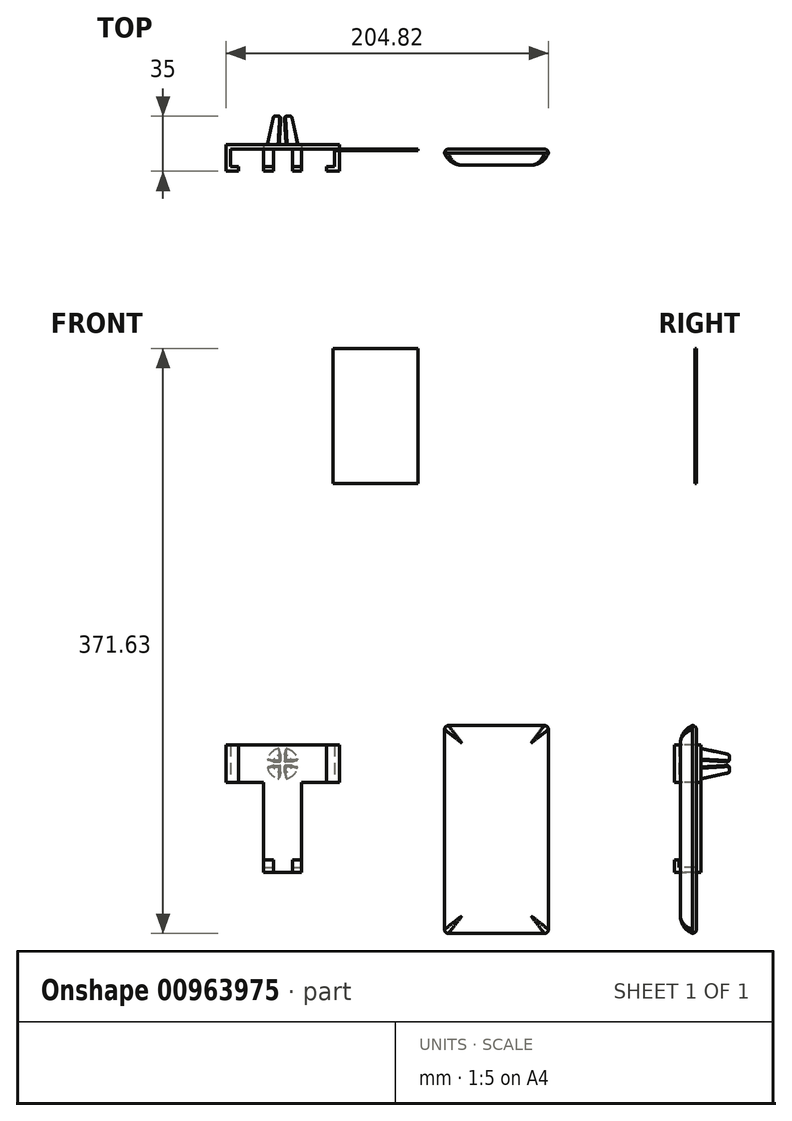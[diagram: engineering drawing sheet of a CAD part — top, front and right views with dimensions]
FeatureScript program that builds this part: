
annotation { "Feature Type Name" : "Feature", "Feature Type Description" : "" }
export const myFeature = defineFeature(function(context is Context, id is Id, definition is map)
    precondition{}
    {
        {
            var Q0;
            Q0=qCreatedBy(makeId("Front.planeOp"),FACE);
            var sketch = newSketch(context, id + "F0", { "sketchPlane" : qUnion([Q0])});
            skCircle(sketch, "E0", {"center": v(0, 0) * mm, "radius": 10 * mm});
            skSolve(sketch);
        }
        {
            var Q0;
            Q0=qSketchRegion(id+"F0",true);
            extrude(context, id + "F1", {"entities" : qUnion([Q0]), "oppositeDirection" : true, "depth" : 3 * mm});
        }
        {
            var Q0;
            Q0=makeQuery(id+"F1.opExtrude","CAP_FACE",FACE,{"disambiguationData":[OSD([sQuery(id+"F0.wireOp",EDGE,"E0")])],"isStart":false});
            var sketch = newSketch(context, id + "F2", { "sketchPlane" : qUnion([Q0])});
            skLineSegment(sketch, "E1.top", {"start": v(-9.75, 2.2) * mm, "end": v(-2.2, 2.2) * mm});
            skLineSegment(sketch, "E1.right", {"start": v(-2.2, 9.75) * mm, "end": v(-2.2, 2.2) * mm});
            skArc(sketch, "E2", {"start": v(-2.2, 9.75) * mm, "mid": v(-7.07, 7.07) * mm, "end": v(-9.75, 2.2) * mm});
            skLineSegment(sketch, "E3.1.0", {"start": v(-9.75, -2.2) * mm, "end": v(-2.2, -2.2) * mm});
            skLineSegment(sketch, "E3.1.1", {"start": v(-2.2, -9.75) * mm, "end": v(-2.2, -2.2) * mm});
            skArc(sketch, "E3.1.2", {"start": v(-9.75, -2.2) * mm, "mid": v(-7.07, -7.07) * mm, "end": v(-2.2, -9.75) * mm});
            skLineSegment(sketch, "E3.2.0", {"start": v(2.2, -9.75) * mm, "end": v(2.2, -2.2) * mm});
            skLineSegment(sketch, "E3.2.1", {"start": v(9.75, -2.2) * mm, "end": v(2.2, -2.2) * mm});
            skArc(sketch, "E3.2.2", {"start": v(2.2, -9.75) * mm, "mid": v(7.07, -7.07) * mm, "end": v(9.75, -2.2) * mm});
            skLineSegment(sketch, "E4.2.3.0", {"start": v(9.75, 2.2) * mm, "end": v(2.2, 2.2) * mm});
            skLineSegment(sketch, "E4.3.3.0", {"start": v(2.2, 9.75) * mm, "end": v(2.2, 2.2) * mm});
            skArc(sketch, "E4.6.3.0", {"start": v(9.75, 2.2) * mm, "mid": v(7.07, 7.07) * mm, "end": v(2.2, 9.75) * mm});
            skSolve(sketch);
        }
        {
            var Q0;
            Q0=makeQuery(id+"F2.imprint","IMPRINT",FACE,{"disambiguationData":[TD([[makeQuery(id+"F2.imprint","IMPRINT",EDGE,{"derivedFrom":sQuery(id+"F2.wireOp",EDGE,"E1.top")}),-1.0]])]});
            cPlane(context, id + "F3", {"entities" : qUnion([Q0]), "cplaneType" : CPlaneType.OFFSET, "offset" : 18 * mm, "width" : 150 * mm, "height" : 150 * mm});
        }
        {
            var Q0;
            Q0=qCreatedBy(id+"F3.planeOp",FACE);
            var sketch = newSketch(context, id + "F4", { "sketchPlane" : qUnion([Q0])});
            skLineSegment(sketch, "E5.top", {"start": v(-5.9, 1.1) * mm, "end": v(-1.1, 1.1) * mm});
            skLineSegment(sketch, "E5.right", {"start": v(-1.1, 5.9) * mm, "end": v(-1.1, 1.1) * mm});
            skArc(sketch, "E6", {"start": v(-1.1, 5.9) * mm, "mid": v(-4.24, 4.24) * mm, "end": v(-5.9, 1.1) * mm});
            skLineSegment(sketch, "E7.1.0", {"start": v(-5.9, -1.1) * mm, "end": v(-1.1, -1.1) * mm});
            skLineSegment(sketch, "E7.1.1", {"start": v(-1.1, -5.9) * mm, "end": v(-1.1, -1.1) * mm});
            skArc(sketch, "E7.1.2", {"start": v(-5.9, -1.1) * mm, "mid": v(-4.24, -4.24) * mm, "end": v(-1.1, -5.9) * mm});
            skLineSegment(sketch, "E7.2.0", {"start": v(1.1, -5.9) * mm, "end": v(1.1, -1.1) * mm});
            skLineSegment(sketch, "E7.2.1", {"start": v(5.9, -1.1) * mm, "end": v(1.1, -1.1) * mm});
            skArc(sketch, "E7.2.2", {"start": v(1.1, -5.9) * mm, "mid": v(4.24, -4.24) * mm, "end": v(5.9, -1.1) * mm});
            skLineSegment(sketch, "E7.3.0", {"start": v(5.9, 1.1) * mm, "end": v(1.1, 1.1) * mm});
            skLineSegment(sketch, "E7.3.1", {"start": v(1.1, 5.9) * mm, "end": v(1.1, 1.1) * mm});
            skArc(sketch, "E7.3.2", {"start": v(5.9, 1.1) * mm, "mid": v(4.24, 4.24) * mm, "end": v(1.1, 5.9) * mm});
            skSolve(sketch);
        }
        {
            var Q1;
            Q1=makeQuery(id+"F4.imprint","IMPRINT",FACE,{"disambiguationData":[TD([[makeQuery(id+"F4.imprint","IMPRINT",EDGE,{"derivedFrom":sQuery(id+"F4.wireOp",EDGE,"E5.top")}),1.0]])]});
            var Q2;
            Q2=makeQuery(id+"F2.imprint","IMPRINT",FACE,{"disambiguationData":[TD([[makeQuery(id+"F2.imprint","IMPRINT",EDGE,{"derivedFrom":sQuery(id+"F2.wireOp",EDGE,"E1.top")}),1.0]])]});
            loft(context, id + "F5", {"operationType" : NewBodyOperationType.ADD, "sheetProfilesArray" : [{ "sheetProfileEntities" : qUnion([Q1]) }, { "sheetProfileEntities" : qUnion([Q2]) }]});
        }
        {
            var Q1;
            Q1=makeQuery(id+"F2.imprint","IMPRINT",FACE,{"disambiguationData":[TD([[makeQuery(id+"F2.imprint","IMPRINT",EDGE,{"derivedFrom":sQuery(id+"F2.wireOp",EDGE,"E4.2.3.0")}),-1.0]])]});
            var Q2;
            Q2=makeQuery(id+"F4.imprint","IMPRINT",FACE,{"disambiguationData":[TD([[makeQuery(id+"F4.imprint","IMPRINT",EDGE,{"derivedFrom":sQuery(id+"F4.wireOp",EDGE,"E7.3.0")}),-1.0]])]});
            loft(context, id + "F6", {"operationType" : NewBodyOperationType.ADD, "sheetProfilesArray" : [{ "sheetProfileEntities" : qUnion([Q1]) }, { "sheetProfileEntities" : qUnion([Q2]) }]});
        }
        {
            var Q1;
            Q1=makeQuery(id+"F2.imprint","IMPRINT",FACE,{"disambiguationData":[TD([[makeQuery(id+"F2.imprint","IMPRINT",EDGE,{"derivedFrom":sQuery(id+"F2.wireOp",EDGE,"E3.1.0")}),-1.0]])]});
            var Q2;
            Q2=makeQuery(id+"F4.imprint","IMPRINT",FACE,{"disambiguationData":[TD([[makeQuery(id+"F4.imprint","IMPRINT",EDGE,{"derivedFrom":sQuery(id+"F4.wireOp",EDGE,"E7.1.0")}),-1.0]])]});
            loft(context, id + "F7", {"operationType" : NewBodyOperationType.ADD, "sheetProfilesArray" : [{ "sheetProfileEntities" : qUnion([Q1]) }, { "sheetProfileEntities" : qUnion([Q2]) }]});
        }
        {
            var Q1;
            Q1=makeQuery(id+"F2.imprint","IMPRINT",FACE,{"disambiguationData":[TD([[makeQuery(id+"F2.imprint","IMPRINT",EDGE,{"derivedFrom":sQuery(id+"F2.wireOp",EDGE,"E3.2.0")}),-1.0]])]});
            var Q2;
            Q2=makeQuery(id+"F4.imprint","IMPRINT",FACE,{"disambiguationData":[TD([[makeQuery(id+"F4.imprint","IMPRINT",EDGE,{"derivedFrom":sQuery(id+"F4.wireOp",EDGE,"E7.2.0")}),-1.0]])]});
            loft(context, id + "F8", {"operationType" : NewBodyOperationType.ADD, "sheetProfilesArray" : [{ "sheetProfileEntities" : qUnion([Q1]) }, { "sheetProfileEntities" : qUnion([Q2]) }]});
        }
        {
            var Q0;
            {var subQ0=sQuery(id+"F4.wireOp",EDGE,"E6");var subQ1=sQuery(id+"F4.wireOp",EDGE,"E5.right");var subQ2=sQuery(id+"F4.wireOp",EDGE,"E5.top");Q0=makeQuery(id+"F5.opLoft","MID_CAP_EDGE",EDGE,{"disambiguationData":[OSD([subQ2,subQ1,subQ0]),TDD([makeQuery(id+"F4.imprint","INTERSECT",VERTEX,{"derivedFrom":[subQ2,subQ0]}),makeQuery(id+"F4.imprint","INTERSECT",VERTEX,{"derivedFrom":[subQ1,subQ0]}),makeQuery(id+"F4.imprint","IMPRINT",EDGE,{"derivedFrom":subQ0})])],"capPos":0.0});}
            var Q1;
            Q1=makeQuery(id+"F5.opLoft","SWEPT_EDGE",EDGE,{"disambiguationData":[OSD([sQuery(id+"F2.wireOp",EDGE,"E1.right"),sQuery(id+"F2.wireOp",EDGE,"E2"),sQuery(id+"F4.wireOp",EDGE,"E5.right"),sQuery(id+"F4.wireOp",EDGE,"E6")])]});
            var Q2;
            Q2=makeQuery(id+"F5.opLoft","SWEPT_EDGE",EDGE,{"disambiguationData":[OSD([sQuery(id+"F2.wireOp",EDGE,"E1.top"),sQuery(id+"F2.wireOp",EDGE,"E1.right"),sQuery(id+"F4.wireOp",EDGE,"E5.top"),sQuery(id+"F4.wireOp",EDGE,"E5.right")])]});
            var Q3;
            Q3=makeQuery(id+"F5.opLoft","SWEPT_EDGE",EDGE,{"disambiguationData":[OSD([sQuery(id+"F2.wireOp",EDGE,"E1.top"),sQuery(id+"F2.wireOp",EDGE,"E2"),sQuery(id+"F4.wireOp",EDGE,"E5.top"),sQuery(id+"F4.wireOp",EDGE,"E6")])]});
            var Q4;
            {var subQ0=sQuery(id+"F4.wireOp",EDGE,"E7.1.2");var subQ1=sQuery(id+"F4.wireOp",EDGE,"E7.1.1");var subQ2=sQuery(id+"F4.wireOp",EDGE,"E7.1.0");Q4=makeQuery(id+"F7.opLoft","MID_CAP_EDGE",EDGE,{"disambiguationData":[OSD([subQ2,subQ1,subQ0]),TDD([makeQuery(id+"F4.imprint","INTERSECT",VERTEX,{"derivedFrom":[subQ2,subQ0]}),makeQuery(id+"F4.imprint","INTERSECT",VERTEX,{"derivedFrom":[subQ1,subQ0]}),makeQuery(id+"F4.imprint","IMPRINT",EDGE,{"derivedFrom":subQ0})])],"capPos":1.0});}
            var Q5;
            Q5=makeQuery(id+"F7.opLoft","SWEPT_EDGE",EDGE,{"disambiguationData":[OSD([sQuery(id+"F2.wireOp",EDGE,"E3.1.0"),sQuery(id+"F2.wireOp",EDGE,"E3.1.2"),sQuery(id+"F4.wireOp",EDGE,"E7.1.0"),sQuery(id+"F4.wireOp",EDGE,"E7.1.2")])]});
            var Q6;
            Q6=makeQuery(id+"F7.opLoft","SWEPT_EDGE",EDGE,{"disambiguationData":[OSD([sQuery(id+"F2.wireOp",EDGE,"E3.1.0"),sQuery(id+"F2.wireOp",EDGE,"E3.1.1"),sQuery(id+"F4.wireOp",EDGE,"E7.1.0"),sQuery(id+"F4.wireOp",EDGE,"E7.1.1")])]});
            var Q7;
            Q7=makeQuery(id+"F7.opLoft","SWEPT_EDGE",EDGE,{"disambiguationData":[OSD([sQuery(id+"F2.wireOp",EDGE,"E3.1.1"),sQuery(id+"F2.wireOp",EDGE,"E3.1.2"),sQuery(id+"F4.wireOp",EDGE,"E7.1.1"),sQuery(id+"F4.wireOp",EDGE,"E7.1.2")])]});
            var Q8;
            {var subQ0=sQuery(id+"F4.wireOp",EDGE,"E7.2.2");var subQ1=sQuery(id+"F4.wireOp",EDGE,"E7.2.1");var subQ2=sQuery(id+"F4.wireOp",EDGE,"E7.2.0");Q8=makeQuery(id+"F8.opLoft","MID_CAP_EDGE",EDGE,{"disambiguationData":[OSD([subQ2,subQ1,subQ0]),TDD([makeQuery(id+"F4.imprint","INTERSECT",VERTEX,{"derivedFrom":[subQ2,subQ0]}),makeQuery(id+"F4.imprint","INTERSECT",VERTEX,{"derivedFrom":[subQ1,subQ0]}),makeQuery(id+"F4.imprint","IMPRINT",EDGE,{"derivedFrom":subQ0})])],"capPos":1.0});}
            var Q9;
            Q9=makeQuery(id+"F8.opLoft","SWEPT_EDGE",EDGE,{"disambiguationData":[OSD([sQuery(id+"F2.wireOp",EDGE,"E3.2.0"),sQuery(id+"F2.wireOp",EDGE,"E3.2.2"),sQuery(id+"F4.wireOp",EDGE,"E7.2.0"),sQuery(id+"F4.wireOp",EDGE,"E7.2.2")])]});
            var Q10;
            Q10=makeQuery(id+"F8.opLoft","SWEPT_EDGE",EDGE,{"disambiguationData":[OSD([sQuery(id+"F2.wireOp",EDGE,"E3.2.1"),sQuery(id+"F2.wireOp",EDGE,"E3.2.2"),sQuery(id+"F4.wireOp",EDGE,"E7.2.1"),sQuery(id+"F4.wireOp",EDGE,"E7.2.2")])]});
            var Q11;
            Q11=makeQuery(id+"F8.opLoft","SWEPT_EDGE",EDGE,{"disambiguationData":[OSD([sQuery(id+"F2.wireOp",EDGE,"E3.2.0"),sQuery(id+"F2.wireOp",EDGE,"E3.2.1"),sQuery(id+"F4.wireOp",EDGE,"E7.2.0"),sQuery(id+"F4.wireOp",EDGE,"E7.2.1")])]});
            var Q12;
            {var subQ0=sQuery(id+"F4.wireOp",EDGE,"E7.3.2");var subQ1=sQuery(id+"F4.wireOp",EDGE,"E7.3.1");var subQ2=sQuery(id+"F4.wireOp",EDGE,"E7.3.0");Q12=makeQuery(id+"F6.opLoft","MID_CAP_EDGE",EDGE,{"disambiguationData":[OSD([subQ2,subQ1,subQ0]),TDD([makeQuery(id+"F4.imprint","INTERSECT",VERTEX,{"derivedFrom":[subQ2,subQ0]}),makeQuery(id+"F4.imprint","INTERSECT",VERTEX,{"derivedFrom":[subQ1,subQ0]}),makeQuery(id+"F4.imprint","IMPRINT",EDGE,{"derivedFrom":subQ0})])],"capPos":1.0});}
            var Q13;
            Q13=makeQuery(id+"F6.opLoft","SWEPT_EDGE",EDGE,{"disambiguationData":[OSD([sQuery(id+"F2.wireOp",EDGE,"E4.2.3.0"),sQuery(id+"F2.wireOp",EDGE,"E4.3.3.0"),sQuery(id+"F4.wireOp",EDGE,"E7.3.0"),sQuery(id+"F4.wireOp",EDGE,"E7.3.1")])]});
            var Q14;
            Q14=makeQuery(id+"F6.opLoft","SWEPT_EDGE",EDGE,{"disambiguationData":[OSD([sQuery(id+"F2.wireOp",EDGE,"E4.2.3.0"),sQuery(id+"F2.wireOp",EDGE,"E4.6.3.0"),sQuery(id+"F4.wireOp",EDGE,"E7.3.0"),sQuery(id+"F4.wireOp",EDGE,"E7.3.2")])]});
            var Q15;
            Q15=makeQuery(id+"F6.opLoft","SWEPT_EDGE",EDGE,{"disambiguationData":[OSD([sQuery(id+"F2.wireOp",EDGE,"E4.3.3.0"),sQuery(id+"F2.wireOp",EDGE,"E4.6.3.0"),sQuery(id+"F4.wireOp",EDGE,"E7.3.1"),sQuery(id+"F4.wireOp",EDGE,"E7.3.2")])]});
            fillet(context, id + "F9", {"entities" : qUnion([Q0, Q1, Q2, Q3, Q4, Q5, Q6, Q7, Q8, Q9, Q10, Q11, Q12, Q13, Q14, Q15]), "radius" : .5 * mm, "tangentPropagation" : true, "allowEdgeOverflow" : false});
        }
        {
            var Q0;
            Q0=qCreatedBy(makeId("Front.planeOp"),FACE);
            var sketch = newSketch(context, id + "F10", { "sketchPlane" : qUnion([Q0])});
            skLineSegment(sketch, "E8.bottom", {"start": v(86.03, 177.78) * mm, "end": v(32.03, 177.78) * mm});
            skLineSegment(sketch, "E8.top", {"start": v(86.03, 263.78) * mm, "end": v(32.03, 263.78) * mm});
            skLineSegment(sketch, "E8.left", {"start": v(86.03, 177.78) * mm, "end": v(86.03, 263.78) * mm});
            skLineSegment(sketch, "E8.right", {"start": v(32.03, 177.78) * mm, "end": v(32.03, 263.78) * mm});
            skSolve(sketch);
        }
        {
            var Q0;
            Q0=makeQuery(id+"F10.imprint","IMPRINT",FACE,{"disambiguationData":[TD([[makeQuery(id+"F10.imprint","IMPRINT",EDGE,{"derivedFrom":sQuery(id+"F10.wireOp",EDGE,"E8.bottom")}),-1.0]])]});
            extrude(context, id + "F11", {"entities" : qUnion([Q0]), "depth" : 1 * mm});
        }
        {
            var Q0;
            {var subQ0=sQuery(id+"F4.wireOp",EDGE,"E5.right");var subQ1=sQuery(id+"F4.wireOp",EDGE,"E6");var subQ2=sQuery(id+"F4.wireOp",EDGE,"E5.top");Q0=makeQuery(id+"F5.opLoft","MID_CAP_EDGE",EDGE,{"disambiguationData":[OSD([subQ2,subQ0,subQ1]),TDD([makeQuery(id+"F4.imprint","INTERSECT",VERTEX,{"derivedFrom":[subQ2,subQ0]}),makeQuery(id+"F4.imprint","INTERSECT",VERTEX,{"derivedFrom":[subQ0,subQ1]}),makeQuery(id+"F4.imprint","IMPRINT",EDGE,{"derivedFrom":subQ0})])],"capPos":0.0});}
            var Q1;
            {var subQ0=sQuery(id+"F4.wireOp",EDGE,"E5.top");var subQ1=sQuery(id+"F4.wireOp",EDGE,"E5.right");var subQ2=sQuery(id+"F4.wireOp",EDGE,"E6");Q1=makeQuery(id+"F5.opLoft","MID_CAP_EDGE",EDGE,{"disambiguationData":[OSD([subQ0,subQ1,subQ2]),TDD([makeQuery(id+"F4.imprint","INTERSECT",VERTEX,{"derivedFrom":[subQ0,subQ2]}),makeQuery(id+"F4.imprint","INTERSECT",VERTEX,{"derivedFrom":[subQ0,subQ1]}),makeQuery(id+"F4.imprint","IMPRINT",EDGE,{"derivedFrom":subQ0})])],"capPos":0.0});}
            var Q2;
            {var subQ0=sQuery(id+"F4.wireOp",EDGE,"E7.1.0");var subQ1=sQuery(id+"F4.wireOp",EDGE,"E7.1.1");var subQ2=sQuery(id+"F4.wireOp",EDGE,"E7.1.2");Q2=makeQuery(id+"F7.opLoft","MID_CAP_EDGE",EDGE,{"disambiguationData":[OSD([subQ0,subQ1,subQ2]),TDD([makeQuery(id+"F4.imprint","INTERSECT",VERTEX,{"derivedFrom":[subQ0,subQ2]}),makeQuery(id+"F4.imprint","INTERSECT",VERTEX,{"derivedFrom":[subQ0,subQ1]}),makeQuery(id+"F4.imprint","IMPRINT",EDGE,{"derivedFrom":subQ0})])],"capPos":1.0});}
            var Q3;
            {var subQ0=sQuery(id+"F4.wireOp",EDGE,"E7.1.1");var subQ1=sQuery(id+"F4.wireOp",EDGE,"E7.1.2");var subQ2=sQuery(id+"F4.wireOp",EDGE,"E7.1.0");Q3=makeQuery(id+"F7.opLoft","MID_CAP_EDGE",EDGE,{"disambiguationData":[OSD([subQ2,subQ0,subQ1]),TDD([makeQuery(id+"F4.imprint","INTERSECT",VERTEX,{"derivedFrom":[subQ2,subQ0]}),makeQuery(id+"F4.imprint","INTERSECT",VERTEX,{"derivedFrom":[subQ0,subQ1]}),makeQuery(id+"F4.imprint","IMPRINT",EDGE,{"derivedFrom":subQ0})])],"capPos":1.0});}
            var Q4;
            {var subQ0=sQuery(id+"F4.wireOp",EDGE,"E7.2.0");var subQ1=sQuery(id+"F4.wireOp",EDGE,"E7.2.1");var subQ2=sQuery(id+"F4.wireOp",EDGE,"E7.2.2");Q4=makeQuery(id+"F8.opLoft","MID_CAP_EDGE",EDGE,{"disambiguationData":[OSD([subQ0,subQ1,subQ2]),TDD([makeQuery(id+"F4.imprint","INTERSECT",VERTEX,{"derivedFrom":[subQ0,subQ2]}),makeQuery(id+"F4.imprint","INTERSECT",VERTEX,{"derivedFrom":[subQ0,subQ1]}),makeQuery(id+"F4.imprint","IMPRINT",EDGE,{"derivedFrom":subQ0})])],"capPos":1.0});}
            var Q5;
            {var subQ0=sQuery(id+"F4.wireOp",EDGE,"E7.2.1");var subQ1=sQuery(id+"F4.wireOp",EDGE,"E7.2.2");var subQ2=sQuery(id+"F4.wireOp",EDGE,"E7.2.0");Q5=makeQuery(id+"F8.opLoft","MID_CAP_EDGE",EDGE,{"disambiguationData":[OSD([subQ2,subQ0,subQ1]),TDD([makeQuery(id+"F4.imprint","INTERSECT",VERTEX,{"derivedFrom":[subQ2,subQ0]}),makeQuery(id+"F4.imprint","INTERSECT",VERTEX,{"derivedFrom":[subQ0,subQ1]}),makeQuery(id+"F4.imprint","IMPRINT",EDGE,{"derivedFrom":subQ0})])],"capPos":1.0});}
            var Q6;
            {var subQ0=sQuery(id+"F4.wireOp",EDGE,"E7.3.0");var subQ1=sQuery(id+"F4.wireOp",EDGE,"E7.3.1");var subQ2=sQuery(id+"F4.wireOp",EDGE,"E7.3.2");Q6=makeQuery(id+"F6.opLoft","MID_CAP_EDGE",EDGE,{"disambiguationData":[OSD([subQ0,subQ1,subQ2]),TDD([makeQuery(id+"F4.imprint","INTERSECT",VERTEX,{"derivedFrom":[subQ0,subQ2]}),makeQuery(id+"F4.imprint","INTERSECT",VERTEX,{"derivedFrom":[subQ0,subQ1]}),makeQuery(id+"F4.imprint","IMPRINT",EDGE,{"derivedFrom":subQ0})])],"capPos":1.0});}
            var Q7;
            {var subQ0=sQuery(id+"F4.wireOp",EDGE,"E7.3.1");var subQ1=sQuery(id+"F4.wireOp",EDGE,"E7.3.2");var subQ2=sQuery(id+"F4.wireOp",EDGE,"E7.3.0");Q7=makeQuery(id+"F6.opLoft","MID_CAP_EDGE",EDGE,{"disambiguationData":[OSD([subQ2,subQ0,subQ1]),TDD([makeQuery(id+"F4.imprint","INTERSECT",VERTEX,{"derivedFrom":[subQ2,subQ0]}),makeQuery(id+"F4.imprint","INTERSECT",VERTEX,{"derivedFrom":[subQ0,subQ1]}),makeQuery(id+"F4.imprint","IMPRINT",EDGE,{"derivedFrom":subQ0})])],"capPos":1.0});}
            fillet(context, id + "F12", {"entities" : qUnion([Q0, Q1, Q2, Q3, Q4, Q5, Q6, Q7]), "radius" : 1.5 * mm, "tangentPropagation" : true, "allowEdgeOverflow" : false});
        }
        {
            var Q0;
            Q0=qCreatedBy(makeId("Front.planeOp"),FACE);
            var sketch = newSketch(context, id + "F13", { "sketchPlane" : qUnion([Q0])});
            skLineSegment(sketch, "E9.bottom", {"start": v(102.82, 24.15) * mm, "end": v(168.82, 24.15) * mm});
            skLineSegment(sketch, "E9.top", {"start": v(102.82, -107.85) * mm, "end": v(168.82, -107.85) * mm});
            skLineSegment(sketch, "E9.left", {"start": v(102.82, 24.15) * mm, "end": v(102.82, -107.85) * mm});
            skLineSegment(sketch, "E9.right", {"start": v(168.82, 24.15) * mm, "end": v(168.82, -107.85) * mm});
            skSolve(sketch);
        }
        {
            var Q0;
            Q0=qSketchRegion(id+"F13",true);
            extrude(context, id + "F14", {"entities" : qUnion([Q0]), "depth" : 10.16 * mm});
        }
        {
            var Q0;
            Q0=makeQuery(id+"F14.opExtrude","SWEPT_EDGE",EDGE,{"disambiguationData":[OSD([sQuery(id+"F13.wireOp",EDGE,"E9.bottom"),sQuery(id+"F13.wireOp",EDGE,"E9.left")])]});
            var Q1;
            Q1=makeQuery(id+"F14.opExtrude","SWEPT_EDGE",EDGE,{"disambiguationData":[OSD([sQuery(id+"F13.wireOp",EDGE,"E9.bottom"),sQuery(id+"F13.wireOp",EDGE,"E9.right")])]});
            var Q2;
            Q2=makeQuery(id+"F14.opExtrude","SWEPT_EDGE",EDGE,{"disambiguationData":[OSD([sQuery(id+"F13.wireOp",EDGE,"E9.top"),sQuery(id+"F13.wireOp",EDGE,"E9.right")])]});
            var Q3;
            Q3=makeQuery(id+"F14.opExtrude","SWEPT_EDGE",EDGE,{"disambiguationData":[OSD([sQuery(id+"F13.wireOp",EDGE,"E9.top"),sQuery(id+"F13.wireOp",EDGE,"E9.left")])]});
            fillet(context, id + "F15", {"entities" : qUnion([Q0, Q1, Q2, Q3]), "radius" : 2.5 * mm, "tangentPropagation" : true, "allowEdgeOverflow" : false});
        }
        {
            var Q0;
            Q0=makeQuery(id+"F14.opExtrude","CAP_EDGE",EDGE,{"disambiguationData":[OSD([sQuery(id+"F13.wireOp",EDGE,"E9.right")])],"isStart":true});
            var Q1;
            Q1=makeQuery(id+"F14.opExtrude","CAP_EDGE",EDGE,{"disambiguationData":[OSD([sQuery(id+"F13.wireOp",EDGE,"E9.bottom")])],"isStart":true});
            var Q2;
            Q2=makeQuery(id+"F14.opExtrude","CAP_EDGE",EDGE,{"disambiguationData":[OSD([sQuery(id+"F13.wireOp",EDGE,"E9.left")])],"isStart":true});
            var Q3;
            Q3=makeQuery(id+"F14.opExtrude","CAP_EDGE",EDGE,{"disambiguationData":[OSD([sQuery(id+"F13.wireOp",EDGE,"E9.top")])],"isStart":true});
            fillet(context, id + "F16", {"entities" : qUnion([Q0, Q1, Q2, Q3]), "radius" : 2.5 * mm, "tangentPropagation" : true, "allowEdgeOverflow" : false});
        }
        {
            var Q0;
            Q0=makeQuery(id+"F14.opExtrude","CAP_EDGE",EDGE,{"disambiguationData":[OSD([sQuery(id+"F13.wireOp",EDGE,"E9.right")])],"isStart":false});
            var Q1;
            Q1=makeQuery(id+"F14.opExtrude","CAP_EDGE",EDGE,{"disambiguationData":[OSD([sQuery(id+"F13.wireOp",EDGE,"E9.bottom")])],"isStart":false});
            var Q2;
            Q2=makeQuery(id+"F14.opExtrude","CAP_EDGE",EDGE,{"disambiguationData":[OSD([sQuery(id+"F13.wireOp",EDGE,"E9.left")])],"isStart":false});
            var Q3;
            Q3=makeQuery(id+"F14.opExtrude","CAP_EDGE",EDGE,{"disambiguationData":[OSD([sQuery(id+"F13.wireOp",EDGE,"E9.top")])],"isStart":false});
            fillet(context, id + "F17", {"entities" : qUnion([Q0, Q1, Q2, Q3]), "radius" : 12 * mm, "tangentPropagation" : true, "allowEdgeOverflow" : false});
        }
        {
            var Q0;
            Q0=qCreatedBy(makeId("Front.planeOp"),FACE);
            var sketch = newSketch(context, id + "F18", { "sketchPlane" : qUnion([Q0])});
            skLineSegment(sketch, "E10.bottom", {"start": v(-12, -66) * mm, "end": v(12, -66) * mm});
            skLineSegment(sketch, "E10.top", {"start": v(-12, 0) * mm, "end": v(12, 0) * mm});
            skLineSegment(sketch, "E10.left", {"start": v(-12, -66) * mm, "end": v(-12, 0) * mm});
            skLineSegment(sketch, "E10.right", {"start": v(12, -66) * mm, "end": v(12, 0) * mm});
            skSolve(sketch);
        }
        {
            var Q0;
            Q0=qSketchRegion(id+"F18",true);
            extrude(context, id + "F19", {"entities" : qUnion([Q0]), "operationType" : NewBodyOperationType.ADD, "oppositeDirection" : true, "offsetDistance" : 25 * mm, "depth" : 3 * mm});
        }
        {
            var Q0;
            Q0=makeQuery(id+"F19.opExtrude","SWEPT_FACE",FACE,{"disambiguationData":[OSD([sQuery(id+"F18.wireOp",EDGE,"E10.bottom")])]});
            var sketch = newSketch(context, id + "F20", { "sketchPlane" : qUnion([Q0])});
            skLineSegment(sketch, "E11.bottom", {"start": v(12, -3) * mm, "end": v(-12, -3) * mm});
            skLineSegment(sketch, "E11.top", {"start": v(12, 11) * mm, "end": v(-12, 11) * mm});
            skLineSegment(sketch, "E11.left", {"start": v(12, -3) * mm, "end": v(12, 11) * mm});
            skLineSegment(sketch, "E11.right", {"start": v(-12, -3) * mm, "end": v(-12, 11) * mm});
            skSolve(sketch);
        }
        {
            var Q0;
            Q0=qSketchRegion(id+"F20",true);
            extrude(context, id + "F21", {"entities" : qUnion([Q0]), "operationType" : NewBodyOperationType.ADD, "depth" : 3 * mm});
        }
        {
            var Q0;
            Q0=qCreatedBy(makeId("Front.planeOp"),FACE);
            var sketch = newSketch(context, id + "F22", { "sketchPlane" : qUnion([Q0])});
            skLineSegment(sketch, "E12.bottom", {"start": v(33, 12) * mm, "end": v(-33, 12) * mm});
            skLineSegment(sketch, "E12.top", {"start": v(33, -12) * mm, "end": v(-33, -12) * mm});
            skLineSegment(sketch, "E12.left", {"start": v(33, 12) * mm, "end": v(33, -12) * mm});
            skLineSegment(sketch, "E12.right", {"start": v(-33, 12) * mm, "end": v(-33, -12) * mm});
            skLineSegment(sketch, "E13", {"start": v(33, 0) * mm, "end": v(-33, 0) * mm, "construction": true});
            skLineSegment(sketch, "E14", {"start": v(0, -12) * mm, "end": v(0, 12) * mm, "construction": true});
            skPoint(sketch, "E15", {"position": v(0, 0) * mm});
            skSolve(sketch);
        }
        {
            var Q0;
            Q0=makeQuery(id+"F22.imprint","IMPRINT",FACE,{"disambiguationData":[TD([[makeQuery(id+"F22.imprint","IMPRINT",EDGE,{"derivedFrom":sQuery(id+"F22.wireOp",EDGE,"E12.bottom")}),1.0]])]});
            extrude(context, id + "F23", {"entities" : qUnion([Q0]), "operationType" : NewBodyOperationType.ADD, "oppositeDirection" : true, "depth" : 3 * mm});
        }
        {
            var Q0;
            Q0=makeQuery(id+"F23.opExtrude","SWEPT_FACE",FACE,{"disambiguationData":[OSD([sQuery(id+"F22.wireOp",EDGE,"E12.right")])]});
            var sketch = newSketch(context, id + "F24", { "sketchPlane" : qUnion([Q0])});
            skLineSegment(sketch, "E16.bottom", {"start": v(-3, 12) * mm, "end": v(11, 12) * mm});
            skLineSegment(sketch, "E16.top", {"start": v(-3, -12) * mm, "end": v(11, -12) * mm});
            skLineSegment(sketch, "E16.left", {"start": v(-3, 12) * mm, "end": v(-3, -12) * mm});
            skLineSegment(sketch, "E16.right", {"start": v(11, 12) * mm, "end": v(11, -12) * mm});
            skSolve(sketch);
        }
        {
            var Q0;
            Q0=qSketchRegion(id+"F24",true);
            extrude(context, id + "F25", {"entities" : qUnion([Q0]), "operationType" : NewBodyOperationType.ADD, "depth" : 3 * mm});
        }
        {
            var Q0;
            Q0=makeQuery(id+"F23.opExtrude","SWEPT_FACE",FACE,{"disambiguationData":[OSD([sQuery(id+"F22.wireOp",EDGE,"E12.left")])]});
            var sketch = newSketch(context, id + "F26", { "sketchPlane" : qUnion([Q0])});
            skLineSegment(sketch, "E17.bottom", {"start": v(3, -12) * mm, "end": v(-11, -12) * mm});
            skLineSegment(sketch, "E17.top", {"start": v(3, 12) * mm, "end": v(-11, 12) * mm});
            skLineSegment(sketch, "E17.left", {"start": v(3, -12) * mm, "end": v(3, 12) * mm});
            skLineSegment(sketch, "E17.right", {"start": v(-11, -12) * mm, "end": v(-11, 12) * mm});
            skSolve(sketch);
        }
        {
            var Q0;
            Q0=qSketchRegion(id+"F26",true);
            extrude(context, id + "F27", {"entities" : qUnion([Q0]), "operationType" : NewBodyOperationType.ADD, "depth" : 3 * mm});
        }
        {
            var Q0;
            Q0=makeQuery(id+"F21.opExtrude","CAP_FACE",FACE,{"disambiguationData":[OSD([sQuery(id+"F20.wireOp",EDGE,"E11.bottom"),sQuery(id+"F20.wireOp",EDGE,"E11.top"),sQuery(id+"F20.wireOp",EDGE,"E11.left"),sQuery(id+"F20.wireOp",EDGE,"E11.right")])],"isStart":false});
            var sketch = newSketch(context, id + "F28", { "sketchPlane" : qUnion([Q0])});
            skLineSegment(sketch, "E18.bottom", {"start": v(-5.84, 11) * mm, "end": v(6.16, 11) * mm});
            skLineSegment(sketch, "E18.top", {"start": v(-5.84, 0) * mm, "end": v(6.16, 0) * mm});
            skLineSegment(sketch, "E18.left", {"start": v(-5.84, 11) * mm, "end": v(-5.84, 0) * mm});
            skLineSegment(sketch, "E18.right", {"start": v(6.16, 11) * mm, "end": v(6.16, 0) * mm});
            skSolve(sketch);
        }
        {
            var Q0;
            Q0=qSketchRegion(id+"F28",true);
            extrude(context, id + "F29", {"entities" : qUnion([Q0]), "operationType" : NewBodyOperationType.REMOVE, "endBound" : BoundingType.UP_TO_NEXT, "oppositeDirection" : true, "depth" : 25 * mm});
        }
        {
            var Q0;
            Q0=makeQuery(id+"F25.opExtrude","SWEPT_FACE",FACE,{"disambiguationData":[OSD([sQuery(id+"F24.wireOp",EDGE,"E16.right")])]});
            var sketch = newSketch(context, id + "F30", { "sketchPlane" : qUnion([Q0])});
            skLineSegment(sketch, "E19.bottom", {"start": v(-36, -12) * mm, "end": v(-28, -12) * mm});
            skLineSegment(sketch, "E19.top", {"start": v(-36, 12) * mm, "end": v(-28, 12) * mm});
            skLineSegment(sketch, "E19.left", {"start": v(-36, -12) * mm, "end": v(-36, 12) * mm});
            skLineSegment(sketch, "E19.right", {"start": v(-28, -12) * mm, "end": v(-28, 12) * mm});
            skLineSegment(sketch, "E20.bottom", {"start": v(36, -12) * mm, "end": v(28, -12) * mm});
            skLineSegment(sketch, "E20.top", {"start": v(36, 12) * mm, "end": v(28, 12) * mm});
            skLineSegment(sketch, "E20.left", {"start": v(36, -12) * mm, "end": v(36, 12) * mm});
            skLineSegment(sketch, "E20.right", {"start": v(28, -12) * mm, "end": v(28, 12) * mm});
            skLineSegment(sketch, "E21.bottom", {"start": v(-12, -69) * mm, "end": v(-5.84, -69) * mm});
            skLineSegment(sketch, "E21.top", {"start": v(-12, -61) * mm, "end": v(-5.84, -61) * mm});
            skLineSegment(sketch, "E21.left", {"start": v(-12, -69) * mm, "end": v(-12, -61) * mm});
            skLineSegment(sketch, "E21.right", {"start": v(-5.84, -69) * mm, "end": v(-5.84, -61) * mm});
            skLineSegment(sketch, "E22.bottom", {"start": v(6.16, -69) * mm, "end": v(12, -69) * mm});
            skLineSegment(sketch, "E22.top", {"start": v(6.16, -61) * mm, "end": v(12, -61) * mm});
            skLineSegment(sketch, "E22.left", {"start": v(6.16, -69) * mm, "end": v(6.16, -61) * mm});
            skLineSegment(sketch, "E22.right", {"start": v(12, -69) * mm, "end": v(12, -61) * mm});
            skSolve(sketch);
        }
        {
            var Q0;
            Q0=qSketchRegion(id+"F30",true);
            extrude(context, id + "F31", {"entities" : qUnion([Q0]), "operationType" : NewBodyOperationType.ADD, "depth" : 3 * mm});
        }
    });
